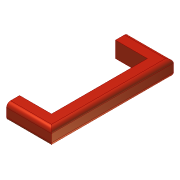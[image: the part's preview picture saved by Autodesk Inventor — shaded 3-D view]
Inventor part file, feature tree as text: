
AUTODESK INVENTOR PART (.ipt)
format: ipt  version: 2012 (Build 160160000, 160)  size: 90,624 bytes
history: native  units: in
note: dims shown in document units (in); Inventor stores cm internally (conversion verified against a paired STEP export)
features: extrude x1, fillet x1, sketch x1
ambient origin geometry x8: Origin, YZ Plane, XZ Plane, XY Plane, X Axis, Y Axis, Z Axis, Center Point
bodies: Solid1 (feature_tree)
feature tree (3):
  extrude  "Extrusion1"  Depth=8.0in
  fillet  "Fillet1"  Radius=3.25in
  sketch  "Sketch2"  dims[d0=3.25in d1=8.0in d2=3.25in d4=24.0in d5=4.0in d6=0.0in d7=1.0in]
